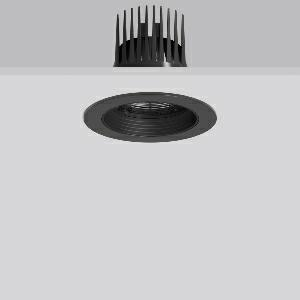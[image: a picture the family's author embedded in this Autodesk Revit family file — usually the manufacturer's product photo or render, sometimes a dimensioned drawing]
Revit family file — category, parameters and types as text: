
# Revit family: heledon_maxi_e_901767_003_76_9490
name_source: partatom
category: Lighting Fixtures
units: mm (PartAtom-declared; Revit-internal decimal feet)

## family parameters
Cut with Voids When Loaded = No
Host = Face
Light Source = No
Part Type = Normal
Room Calculation Point = No
Round Connector Dimension = Use Diameter
Shared = No

## types (1)
- HELEDON maxi E (1 x LED Modul 930, 3650 lm, 3000)
    Apparent Load = 35 VA
    Approval mark = CE
    CIE Flux Codes = 97 100 100 100 100
    Color Rendering = 90
    Color Temperature = 3000
    Default Elevation = 1800 mm
    Description = Series: HELEDON maxi
Round recessed downlight. Housing: die-cast aluminium, powder-coated. Black plastic ring and recessed LED to prevent glare from the side. Optical assembly with lens made of plastic (polycarbonate) for the best homogeneous light distribution - can be changed without tools. Best colour rendering index Ra>90. Suitable for Recessed ceiling mounting. Installation without tools thanks to spring fastening system. Including separate LED converter with connecting cable 600 mm.High quality converter without flickering and stroboscopic effect. Through-wiring box (5 pole) available as accessory. The following accessories can be mounted without use of tools: interchangeable lenses, decorative glasses, honeycomb louvre, clear and frosted diffusers, white interchangeable plastic ring. 
Colour: deep black, matt (RAL 9005)
Diameter: 162 mm
Height: 3 mm
Cut-out diameter: 152 mm
Recess height: 200 mm
Luminaire: recess height: 135 mm
Lamp: LED
Socket: without socket
Colour temperature: 3000K
Colour rendering index (CRI): 92
System power: 35 W
Rated luminous flux: 3650 lm
Luminous efficiency: 104 lm/W
Control gear: Converter, dimmable, DALI
Protection class: II
Type of protection: IP 20
    Height = 0 mm  [stored 0 ft]
    Lamp = 1 x LED Modul 930
    Lamp Light Flux = 3650 lm
    Lamp count = 1
    Length = 162 mm
    Lifetime = 50000 h
    Luminous efficacy = 104 lm/W
    Manufacturer = RZB
    ModVariant = No
    Model = 901767.003.76
    Mounting Place = Ceiling
    Mounting Type = Recessed
    Number of Poles = 1
    OnlyDefault = Yes
    Power Factor = 1
    Product Name = HELEDON maxi E
    Product group = Recessed downlights
    ProductGroupID = 402
    Protection Class = Protection class II
    Protection Degree = IP 20
    RLX_Detail_Level = 1
    RLX_Emergency_Light_Flux = 0 lm
    RLX_Emergency_Type = 0
    RLX_Emergency_Type_DB = No
    RlxData = <blob elided: 122877 chars, md5=b1e4ed48>
    Socket = socket
    Standby Power = 0 W
    System Light Flux = 3650 lm
    System Power = 35 W
    Type Comments = Product without accessories
    Type Image = 901663.003.jpg
    URL = http://relux.com
    VarID = ---
    Voltage = 230 V
    Voltage Range = 220-240 V
    Weight = 0.00 kg
    Width = 0 mm  [stored 0 ft]

note: [stored X ft] marks values corroborated as IEEE doubles in the binary element streams (Revit-internal decimal feet)

## geometry (parser evidence)
native form markers: Blend x4, Sweep x13
no freeform markers — native parametric forms only
